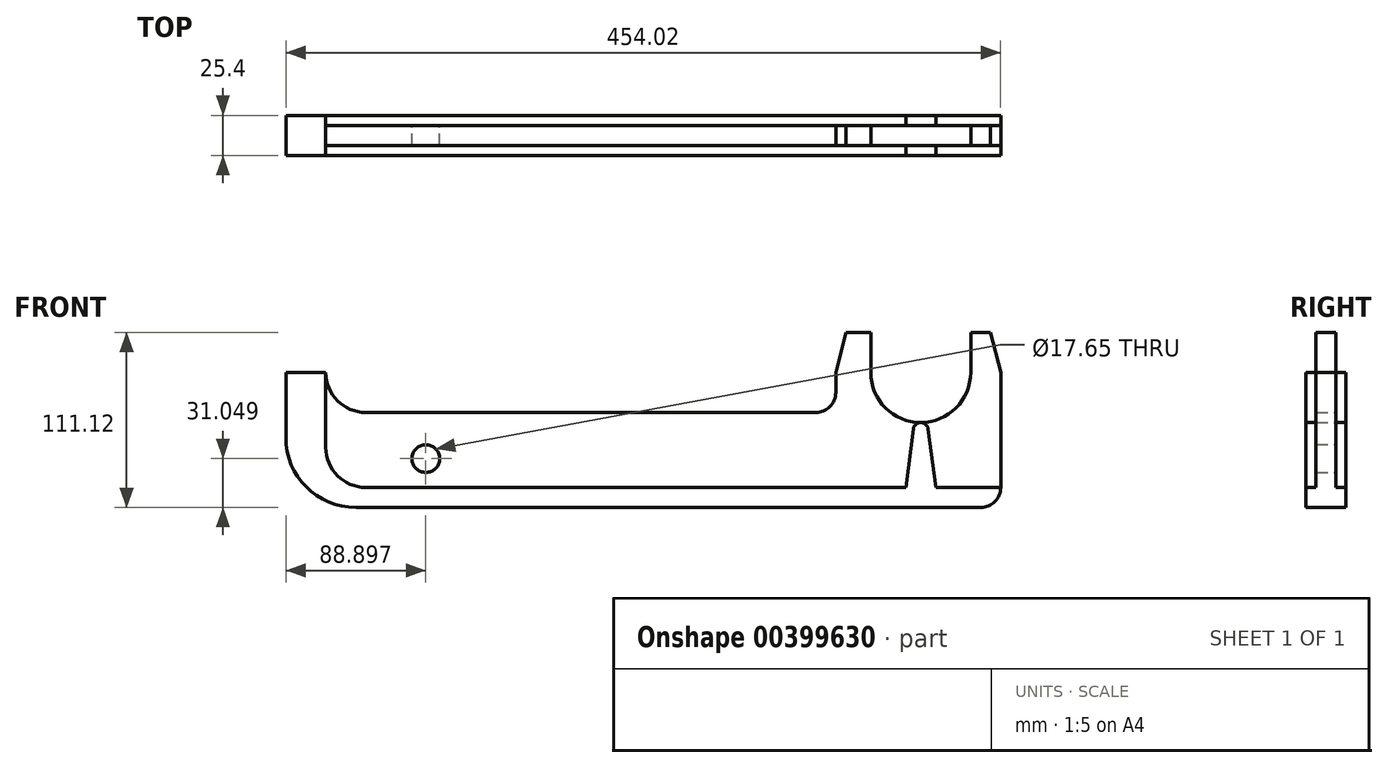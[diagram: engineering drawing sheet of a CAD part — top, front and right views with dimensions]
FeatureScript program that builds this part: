
annotation { "Feature Type Name" : "Feature", "Feature Type Description" : "" }
export const myFeature = defineFeature(function(context is Context, id is Id, definition is map)
    precondition{}
    {
        {
            var Q0;
            Q0=qCreatedBy(makeId("Front.planeOp"),FACE);
            var sketch = newSketch(context, id + "F0", { "sketchPlane" : qUnion([Q0])});
            skLineSegment(sketch, "E0.bottom", {"start": v(220.66, 55.56) * mm, "end": v(207.96, 55.56) * mm});
            skLineSegment(sketch, "E0.top", {"start": v(214.31, -55.56) * mm, "end": v(-182.56, -55.56) * mm});
            skLineSegment(sketch, "E0.left", {"start": v(227.01, 30.16) * mm, "end": v(227.01, -42.86) * mm});
            skLineSegment(sketch, "E0.right", {"start": v(-227.01, 30.16) * mm, "end": v(-227.01, -11.11) * mm});
            skPoint(sketch, "E0.middle", {"position": v(0, 0) * mm});
            skLineSegment(sketch, "E1", {"start": v(220.66, 55.56) * mm, "end": v(227.01, 30.16) * mm});
            skPoint(sketch, "E2.start.orphan", {"position": v(207.96, 55.56) * mm});
            skLineSegment(sketch, "E3", {"start": v(207.96, 55.56) * mm, "end": v(207.96, 30.16) * mm});
            skLineSegment(sketch, "E4", {"start": v(176.21, -1.59) * mm, "end": v(176.21, -1.59) * mm});
            skLineSegment(sketch, "E5", {"start": v(144.46, 30.16) * mm, "end": v(144.46, 55.56) * mm});
            skLineSegment(sketch, "E6", {"start": v(128.59, 55.56) * mm, "end": v(122.24, 30.16) * mm});
            skLineSegment(sketch, "E7", {"start": v(122.24, 30.16) * mm, "end": v(122.24, 17.46) * mm});
            skLineSegment(sketch, "E8", {"start": v(109.54, 4.76) * mm, "end": v(-176.21, 4.76) * mm});
            skPoint(sketch, "E9.visualSharp", {"position": v(122.24, 4.76) * mm});
            skArc(sketch, "E9.filletArc", {"start": v(109.54, 4.76) * mm, "mid": v(118.52, 8.48) * mm, "end": v(122.24, 17.46) * mm});
            skPoint(sketch, "E10.visualSharp", {"position": v(-201.61, 4.76) * mm});
            skArc(sketch, "E10.filletArc", {"start": v(-201.61, 30.16) * mm, "mid": v(-194.17, 12.2) * mm, "end": v(-176.21, 4.76) * mm});
            skLineSegment(sketch, "E11", {"start": v(-201.61, 30.16) * mm, "end": v(-227.01, 30.16) * mm});
            skPoint(sketch, "E12.visualSharp", {"position": v(207.96, -1.59) * mm});
            skArc(sketch, "E12.filletArc", {"start": v(176.21, -1.59) * mm, "mid": v(198.66, 7.71) * mm, "end": v(207.96, 30.16) * mm});
            skPoint(sketch, "E13.visualSharp", {"position": v(144.46, -1.59) * mm});
            skArc(sketch, "E13.filletArc", {"start": v(144.46, 30.16) * mm, "mid": v(153.76, 7.71) * mm, "end": v(176.21, -1.59) * mm});
            skLineSegment(sketch, "E14.trimOffspring", {"start": v(144.46, 55.56) * mm, "end": v(128.59, 55.56) * mm});
            skPoint(sketch, "E15.orphan", {"position": v(227.01, 55.56) * mm});
            skPoint(sketch, "E16.visualSharp", {"position": v(227.01, -55.56) * mm});
            skArc(sketch, "E16.filletArc", {"start": v(214.31, -55.56) * mm, "mid": v(223.3, -51.84) * mm, "end": v(227.01, -42.86) * mm});
            skPoint(sketch, "E17.visualSharp", {"position": v(-227.01, -55.56) * mm});
            skArc(sketch, "E17.filletArc", {"start": v(-227.01, -11.11) * mm, "mid": v(-214, -42.54) * mm, "end": v(-182.56, -55.56) * mm});
            skCircle(sketch, "E18", {"center": v(-138.11, -24.51) * mm, "radius": 8.83 * mm});
            skSolve(sketch);
        }
        {
            var Q0;
            Q0=makeQuery(id+"F0.imprint","IMPRINT",FACE,{"disambiguationData":[TD([[makeQuery(id+"F0.imprint","IMPRINT",EDGE,{"derivedFrom":sQuery(id+"F0.wireOp",EDGE,"E0.bottom")}),1.0]])]});
            extrude(context, id + "F1", {"entities" : qUnion([Q0]), "depth" : 12.7 * mm});
        }
        {
            var Q0;
            Q0=makeQuery(id+"F1.opExtrude","CAP_FACE",FACE,{"disambiguationData":[OSD([sQuery(id+"F0.wireOp",EDGE,"E0.bottom"),sQuery(id+"F0.wireOp",EDGE,"E0.top"),sQuery(id+"F0.wireOp",EDGE,"E0.left"),sQuery(id+"F0.wireOp",EDGE,"E0.right"),sQuery(id+"F0.wireOp",EDGE,"E1"),sQuery(id+"F0.wireOp",EDGE,"E3"),sQuery(id+"F0.wireOp",EDGE,"E5"),sQuery(id+"F0.wireOp",EDGE,"E6"),sQuery(id+"F0.wireOp",EDGE,"E7"),sQuery(id+"F0.wireOp",EDGE,"E8"),sQuery(id+"F0.wireOp",EDGE,"E9.filletArc"),sQuery(id+"F0.wireOp",EDGE,"E10.filletArc"),sQuery(id+"F0.wireOp",EDGE,"E11"),sQuery(id+"F0.wireOp",EDGE,"E12.filletArc"),sQuery(id+"F0.wireOp",EDGE,"E13.filletArc"),sQuery(id+"F0.wireOp",EDGE,"E14.trimOffspring"),sQuery(id+"F0.wireOp",EDGE,"E16.filletArc"),sQuery(id+"F0.wireOp",EDGE,"E17.filletArc"),sQuery(id+"F0.wireOp",EDGE,"E18")])],"isStart":false});
            var sketch = newSketch(context, id + "F2", { "sketchPlane" : qUnion([Q0])});
            skLineSegment(sketch, "E19", {"start": v(-201.61, 30.16) * mm, "end": v(-201.61, -17.46) * mm});
            skLineSegment(sketch, "E20", {"start": v(-176.21, -42.86) * mm, "end": v(166.69, -42.86) * mm});
            skArc(sketch, "E21", {"start": v(180.94, -5.74) * mm, "mid": v(176.21, -1.59) * mm, "end": v(171.49, -5.74) * mm});
            skLineSegment(sketch, "E22", {"start": v(166.69, -42.86) * mm, "end": v(171.49, -5.74) * mm});
            skLineSegment(sketch, "E23", {"start": v(185.74, -42.86) * mm, "end": v(180.94, -5.74) * mm});
            skLineSegment(sketch, "E24", {"start": v(185.74, -42.86) * mm, "end": v(227.01, -42.86) * mm});
            skPoint(sketch, "E25.orphan", {"position": v(176.21, -1.59) * mm});
            skPoint(sketch, "E26.start.orphan", {"position": v(176.21, -42.86) * mm});
            skPoint(sketch, "E27.visualSharp", {"position": v(-201.61, -42.86) * mm});
            skArc(sketch, "E27.filletArc", {"start": v(-201.61, -17.46) * mm, "mid": v(-194.17, -35.42) * mm, "end": v(-176.21, -42.86) * mm});
            skLineSegment(sketch, "E28", {"start": v(-201.61, 30.16) * mm, "end": v(-227.01, 30.16) * mm});
            skLineSegment(sketch, "E29", {"start": v(-227.01, 30.16) * mm, "end": v(-227.01, -11.11) * mm});
            skLineSegment(sketch, "E30", {"start": v(-182.56, -55.56) * mm, "end": v(214.31, -55.56) * mm});
            skLineSegment(sketch, "E31", {"start": v(227.01, -42.86) * mm, "end": v(227.01, -42.86) * mm});
            skPoint(sketch, "E32.visualSharp", {"position": v(227.01, -55.56) * mm});
            skArc(sketch, "E32.filletArc", {"start": v(214.31, -55.56) * mm, "mid": v(223.3, -51.84) * mm, "end": v(227.01, -42.86) * mm});
            skPoint(sketch, "E33.visualSharp", {"position": v(-227.01, -55.56) * mm});
            skArc(sketch, "E33.filletArc", {"start": v(-227.01, -11.11) * mm, "mid": v(-214, -42.54) * mm, "end": v(-182.56, -55.56) * mm});
            skSolve(sketch);
        }
        {
            var Q0;
            Q0 = qSketchRegion(id + "F2", true);
            extrude(context, id + "F3", {"entities" : qUnion([Q0]), "operationType" : NewBodyOperationType.ADD, "depth" : 6.35 * mm, "hasSecondDirection" : true, "secondDirectionOppositeDirection" : true, "secondDirectionDepth" : 19.05 * mm});
        }
    });
